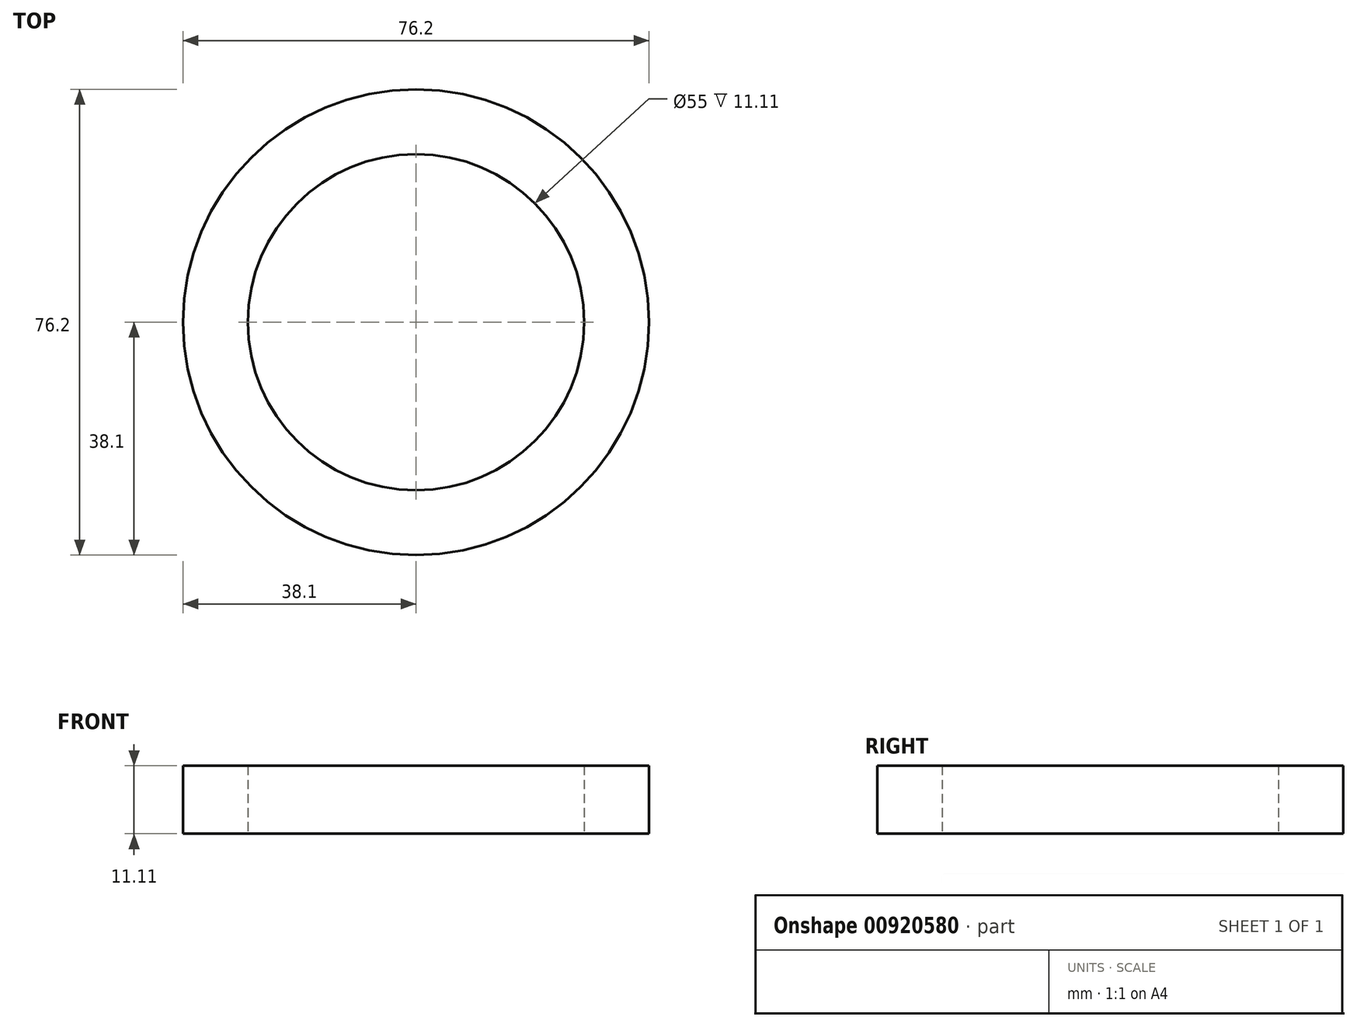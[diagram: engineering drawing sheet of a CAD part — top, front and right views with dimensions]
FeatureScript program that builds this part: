
annotation { "Feature Type Name" : "Feature", "Feature Type Description" : "" }
export const myFeature = defineFeature(function(context is Context, id is Id, definition is map)
    precondition{}
    {
        {
            var Q0;
            Q0=qCreatedBy(makeId("Top.planeOp"),FACE);
            var sketch = newSketch(context, id + "F0", { "sketchPlane" : qUnion([Q0])});
            skCircle(sketch, "E0", {"center": v(0, 0) * mm, "radius": 38.1 * mm});
            skCircle(sketch, "E1", {"center": v(0, 0) * mm, "radius": 27.5 * mm});
            skSolve(sketch);
        }
        {
            var Q0;
            Q0=makeQuery(id+"F0.imprint","IMPRINT",FACE,{"disambiguationData":[TD([[makeQuery(id+"F0.imprint","IMPRINT",EDGE,{"derivedFrom":sQuery(id+"F0.wireOp",EDGE,"E0")}),1.0]])]});
            extrude(context, id + "F1", {"entities" : qUnion([Q0]), "depth" : 11.1 * mm, "offsetDistance" : 25 * mm});
        }
    });
